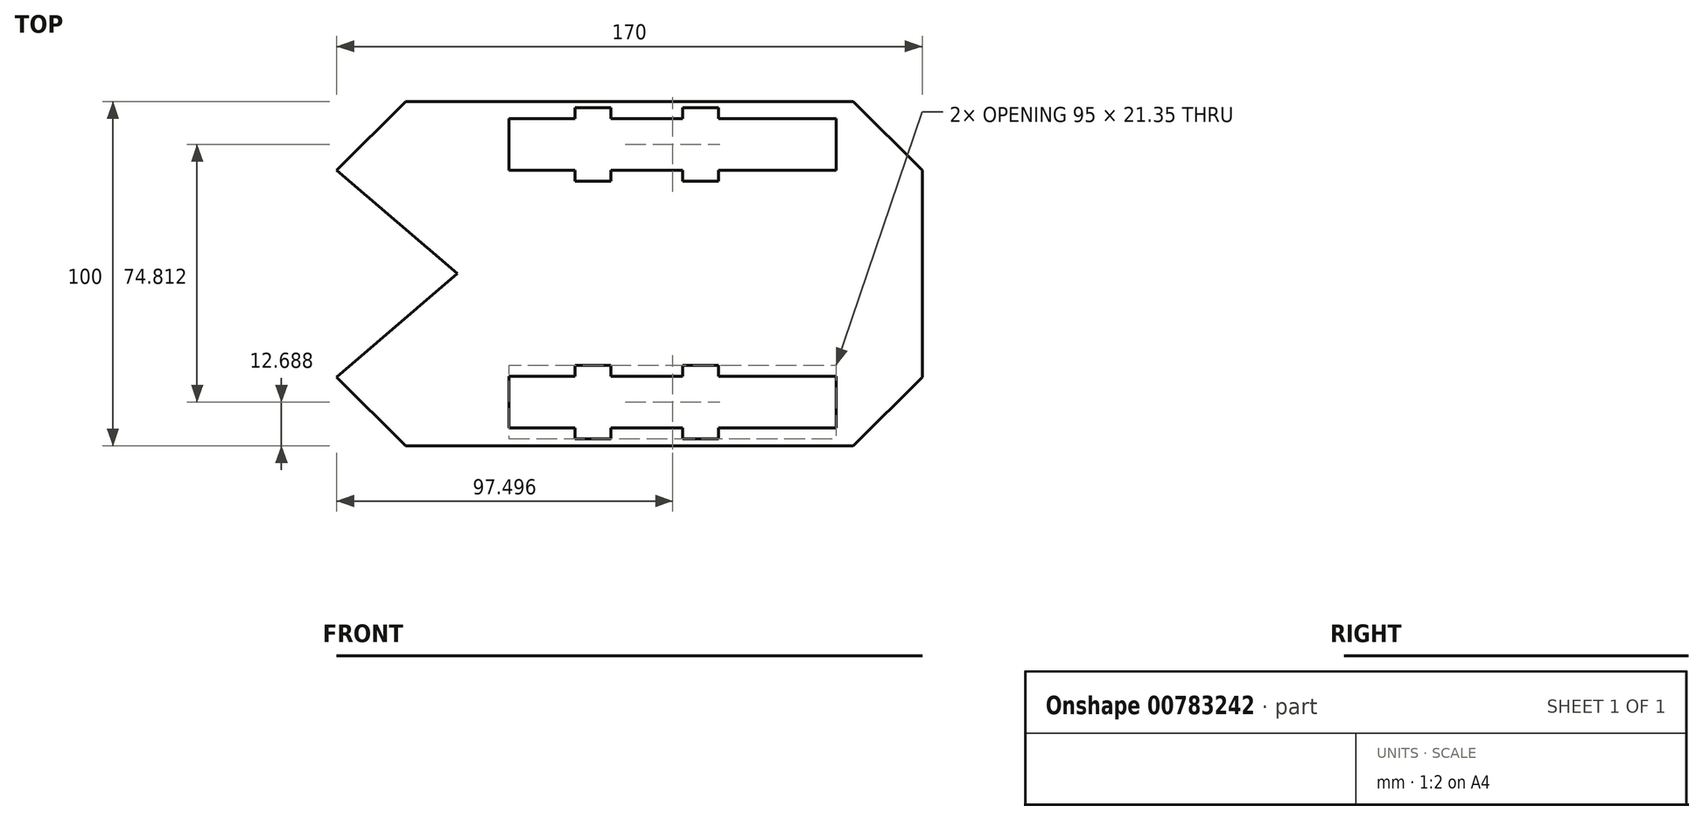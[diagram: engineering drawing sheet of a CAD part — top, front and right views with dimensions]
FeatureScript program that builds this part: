
annotation { "Feature Type Name" : "Feature", "Feature Type Description" : "" }
export const myFeature = defineFeature(function(context is Context, id is Id, definition is map)
    precondition{}
    {
        {
            var Q0;
            Q0=qCreatedBy(makeId("Top.planeOp"),FACE);
            var sketch = newSketch(context, id + "F0", { "sketchPlane" : qUnion([Q0])});
            skLineSegment(sketch, "E0.bottom", {"start": v(-45.53, 81.87) * mm, "end": v(84.47, 81.87) * mm});
            skLineSegment(sketch, "E0.top", {"start": v(-45.53, -18.13) * mm, "end": v(84.47, -18.13) * mm});
            skLineSegment(sketch, "E0.right", {"start": v(104.47, 61.87) * mm, "end": v(104.47, 1.87) * mm});
            skLineSegment(sketch, "E1", {"start": v(104.47, 61.87) * mm, "end": v(84.47, 81.87) * mm});
            skLineSegment(sketch, "E2", {"start": v(104.47, 1.87) * mm, "end": v(84.47, -18.13) * mm});
            skLineSegment(sketch, "E3", {"start": v(-45.53, -18.13) * mm, "end": v(-65.53, 1.87) * mm});
            skLineSegment(sketch, "E4", {"start": v(-65.53, 61.87) * mm, "end": v(-45.53, 81.87) * mm});
            skPoint(sketch, "E5.orphan", {"position": v(104.47, -18.13) * mm});
            skPoint(sketch, "E6.orphan", {"position": v(104.47, 81.87) * mm});
            skPoint(sketch, "E7.orphan", {"position": v(-65.53, 81.87) * mm});
            skPoint(sketch, "E8.start.orphan", {"position": v(104.47, 31.87) * mm});
            skLineSegment(sketch, "E9.bottom", {"start": v(-15.53, 2.06) * mm, "end": v(3.62, 2.06) * mm});
            skLineSegment(sketch, "E9.top", {"start": v(-15.53, -12.94) * mm, "end": v(3.62, -12.94) * mm});
            skLineSegment(sketch, "E9.left", {"start": v(-15.53, 2.06) * mm, "end": v(-15.53, -12.94) * mm});
            skLineSegment(sketch, "E10.bottom", {"start": v(-15.53, 76.87) * mm, "end": v(3.62, 76.87) * mm});
            skLineSegment(sketch, "E10.top", {"start": v(-15.53, 61.87) * mm, "end": v(3.62, 61.87) * mm});
            skLineSegment(sketch, "E10.left", {"start": v(-15.53, 76.87) * mm, "end": v(-15.53, 61.87) * mm});
            skPoint(sketch, "E11.top.start.orphan", {"position": v(-40.53, 4.37) * mm});
            skLineSegment(sketch, "E12", {"start": v(-30.53, 31.87) * mm, "end": v(-65.53, 61.87) * mm});
            skLineSegment(sketch, "E13", {"start": v(-30.53, 31.87) * mm, "end": v(-65.53, 1.87) * mm});
            skLineSegment(sketch, "E14.top", {"start": v(3.62, 58.7) * mm, "end": v(14.05, 58.7) * mm});
            skLineSegment(sketch, "E14.left", {"start": v(3.62, 61.87) * mm, "end": v(3.62, 58.7) * mm});
            skLineSegment(sketch, "E14.right", {"start": v(14.05, 61.87) * mm, "end": v(14.05, 58.7) * mm});
            skLineSegment(sketch, "E15.top", {"start": v(34.88, 58.7) * mm, "end": v(45.3, 58.7) * mm});
            skLineSegment(sketch, "E15.left", {"start": v(34.88, 61.87) * mm, "end": v(34.88, 58.7) * mm});
            skLineSegment(sketch, "E15.right", {"start": v(45.3, 62.06) * mm, "end": v(45.3, 58.7) * mm});
            skLineSegment(sketch, "E16.trimOffspring", {"start": v(45.3, 61.87) * mm, "end": v(64.47, 61.87) * mm});
            skLineSegment(sketch, "E17", {"start": v(14.05, 61.87) * mm, "end": v(34.88, 61.87) * mm});
            skLineSegment(sketch, "E18.top", {"start": v(3.62, 80.05) * mm, "end": v(14.05, 80.05) * mm});
            skLineSegment(sketch, "E18.left", {"start": v(3.62, 76.87) * mm, "end": v(3.62, 80.05) * mm});
            skLineSegment(sketch, "E18.right", {"start": v(14.05, 76.87) * mm, "end": v(14.05, 80.05) * mm});
            skLineSegment(sketch, "E19.top", {"start": v(34.88, 80.05) * mm, "end": v(45.3, 80.05) * mm});
            skLineSegment(sketch, "E19.left", {"start": v(34.88, 76.87) * mm, "end": v(34.88, 80.05) * mm});
            skLineSegment(sketch, "E19.right", {"start": v(45.3, 76.87) * mm, "end": v(45.3, 80.05) * mm});
            skLineSegment(sketch, "E20.trimOffspring", {"start": v(14.05, 76.87) * mm, "end": v(34.88, 76.87) * mm});
            skLineSegment(sketch, "E21.trimOffspring", {"start": v(45.3, 76.87) * mm, "end": v(64.47, 76.87) * mm});
            skLineSegment(sketch, "E22.top", {"start": v(3.62, 5.23) * mm, "end": v(14.05, 5.23) * mm});
            skLineSegment(sketch, "E22.left", {"start": v(3.62, 2.06) * mm, "end": v(3.62, 5.23) * mm});
            skLineSegment(sketch, "E22.right", {"start": v(14.05, 2.06) * mm, "end": v(14.05, 5.23) * mm});
            skLineSegment(sketch, "E23.top", {"start": v(34.88, 5.23) * mm, "end": v(45.3, 5.23) * mm});
            skLineSegment(sketch, "E23.left", {"start": v(34.88, 2.06) * mm, "end": v(34.88, 5.23) * mm});
            skLineSegment(sketch, "E23.right", {"start": v(45.3, 2.06) * mm, "end": v(45.3, 5.23) * mm});
            skLineSegment(sketch, "E24.top", {"start": v(3.62, -16.12) * mm, "end": v(14.05, -16.12) * mm});
            skLineSegment(sketch, "E24.left", {"start": v(3.62, -12.94) * mm, "end": v(3.62, -16.12) * mm});
            skLineSegment(sketch, "E24.right", {"start": v(14.05, -12.94) * mm, "end": v(14.05, -16.12) * mm});
            skLineSegment(sketch, "E25.top", {"start": v(34.88, -16.12) * mm, "end": v(45.3, -16.12) * mm});
            skLineSegment(sketch, "E25.left", {"start": v(34.88, -12.94) * mm, "end": v(34.88, -16.12) * mm});
            skLineSegment(sketch, "E25.right", {"start": v(45.3, -12.94) * mm, "end": v(45.3, -16.12) * mm});
            skLineSegment(sketch, "E26.trimOffspring", {"start": v(14.05, -12.94) * mm, "end": v(34.88, -12.94) * mm});
            skLineSegment(sketch, "E27.trimOffspring", {"start": v(14.05, 2.06) * mm, "end": v(34.88, 2.06) * mm});
            skLineSegment(sketch, "E28.trimOffspring", {"start": v(45.3, 2.06) * mm, "end": v(64.47, 2.06) * mm});
            skLineSegment(sketch, "E29.trimOffspring", {"start": v(45.3, -12.94) * mm, "end": v(64.47, -12.94) * mm});
            skLineSegment(sketch, "E30", {"start": v(64.47, 2.06) * mm, "end": v(74.47, 2.06) * mm});
            skLineSegment(sketch, "E31", {"start": v(74.47, 2.06) * mm, "end": v(74.47, -12.94) * mm});
            skLineSegment(sketch, "E32", {"start": v(64.47, -12.94) * mm, "end": v(74.47, -12.94) * mm});
            skLineSegment(sketch, "E33", {"start": v(64.47, 76.87) * mm, "end": v(74.47, 76.87) * mm});
            skLineSegment(sketch, "E34", {"start": v(74.47, 76.87) * mm, "end": v(74.47, 61.87) * mm});
            skLineSegment(sketch, "E35", {"start": v(64.47, 61.87) * mm, "end": v(74.47, 61.87) * mm});
            skLineSegment(sketch, "E36.bottom", {"start": v(74.47, 76.87) * mm, "end": v(79.47, 76.87) * mm});
            skLineSegment(sketch, "E36.top", {"start": v(74.47, 61.87) * mm, "end": v(79.47, 61.87) * mm});
            skLineSegment(sketch, "E36.right", {"start": v(79.47, 76.87) * mm, "end": v(79.47, 61.87) * mm});
            skLineSegment(sketch, "E37.bottom", {"start": v(74.47, 2.06) * mm, "end": v(79.47, 2.06) * mm});
            skLineSegment(sketch, "E37.top", {"start": v(74.47, -12.94) * mm, "end": v(79.47, -12.94) * mm});
            skLineSegment(sketch, "E37.right", {"start": v(79.47, 2.06) * mm, "end": v(79.47, -12.94) * mm});
            skSolve(sketch);
        }
        {
            var Q0;
            Q0 = qSketchRegion(id + "F0", true);
            extrude(context, id + "F1", {"entities" : qUnion([Q0]), "depth" : 1 / 203.2 * mm, "offsetDistance" : 25.4 * mm});
        }
    });
